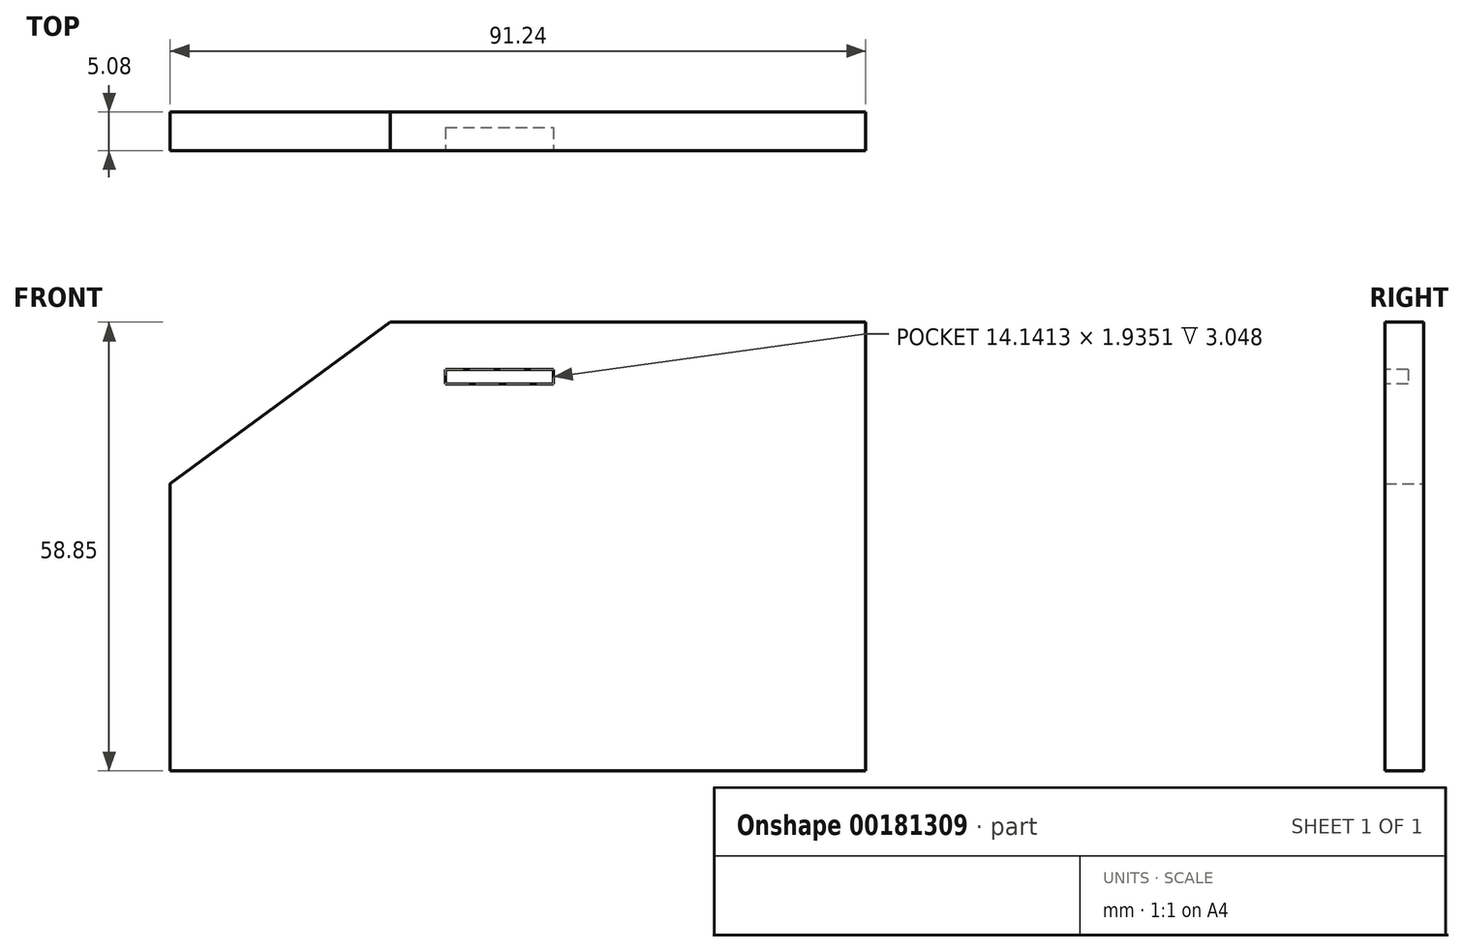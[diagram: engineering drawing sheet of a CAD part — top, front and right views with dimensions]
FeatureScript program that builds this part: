
annotation { "Feature Type Name" : "Feature", "Feature Type Description" : "" }
export const myFeature = defineFeature(function(context is Context, id is Id, definition is map)
    precondition{}
    {
        {
            var Q0;
            Q0=qCreatedBy(makeId("Front.planeOp"),FACE);
            var sketch = newSketch(context, id + "F0", { "sketchPlane" : qUnion([Q0])});
            skLineSegment(sketch, "E0", {"start": v(-53.99, 30.3) * mm, "end": v(-53.99, -7.33) * mm});
            skLineSegment(sketch, "E1", {"start": v(-53.99, 30.3) * mm, "end": v(4.93, 30.3) * mm});
            skLineSegment(sketch, "E2", {"start": v(4.93, 30.3) * mm, "end": v(4.93, -7.33) * mm});
            skLineSegment(sketch, "E3", {"start": v(-53.99, -7.33) * mm, "end": v(4.93, -7.33) * mm});
            skLineSegment(sketch, "E4", {"start": v(4.93, 30.3) * mm, "end": v(37.25, 30.3) * mm});
            skLineSegment(sketch, "E5", {"start": v(4.93, -7.33) * mm, "end": v(37.25, -7.33) * mm});
            skPoint(sketch, "E6.end.orphan", {"position": v(38.16, -7.33) * mm});
            skLineSegment(sketch, "E7", {"start": v(37.25, -7.33) * mm, "end": v(37.25, 30.3) * mm});
            skLineSegment(sketch, "E8", {"start": v(-53.99, 30.3) * mm, "end": v(-25.15, 51.52) * mm});
            skLineSegment(sketch, "E9", {"start": v(-25.15, 51.52) * mm, "end": v(4.93, 30.3) * mm});
            skLineSegment(sketch, "E10", {"start": v(37.25, 30.3) * mm, "end": v(37.25, 51.52) * mm});
            skPoint(sketch, "E11.end.orphan", {"position": v(32.6, 51.52) * mm});
            skLineSegment(sketch, "E12", {"start": v(37.25, 51.52) * mm, "end": v(-25.15, 51.52) * mm});
            skSolve(sketch);
        }
        {
            var Q0;
            Q0=makeQuery(id+"F0.imprint","IMPRINT",FACE,{"disambiguationData":[TD([[makeQuery(id+"F0.imprint","IMPRINT",EDGE,{"derivedFrom":sQuery(id+"F0.wireOp",EDGE,"E1")}),1.0]])]});
            var Q1;
            Q1=makeQuery(id+"F0.imprint","IMPRINT",FACE,{"disambiguationData":[TD([[makeQuery(id+"F0.imprint","IMPRINT",EDGE,{"derivedFrom":sQuery(id+"F0.wireOp",EDGE,"E4")}),1.0]])]});
            var Q2;
            Q2=makeQuery(id+"F0.imprint","IMPRINT",FACE,{"disambiguationData":[TD([[makeQuery(id+"F0.imprint","IMPRINT",EDGE,{"derivedFrom":sQuery(id+"F0.wireOp",EDGE,"E0")}),1.0]])]});
            var Q3;
            Q3=makeQuery(id+"F0.imprint","IMPRINT",FACE,{"disambiguationData":[TD([[makeQuery(id+"F0.imprint","IMPRINT",EDGE,{"derivedFrom":sQuery(id+"F0.wireOp",EDGE,"E2")}),1.0]])]});
            extrude(context, id + "F1", {"entities" : qUnion([Q0, Q1, Q2, Q3]), "depth" : 2.54 * mm, "hasSecondDirection" : true, "secondDirectionOppositeDirection" : true, "secondDirectionDepth" : 2.54 * mm});
        }
        {
            var Q0;
            Q0=makeQuery(id+"F1.opExtrude","SWEPT_FACE",FACE,{"disambiguationData":[OSD([sQuery(id+"F0.wireOp",EDGE,"E3"),sQuery(id+"F0.wireOp",EDGE,"E5")])]});
            var sketch = newSketch(context, id + "F2", { "sketchPlane" : qUnion([Q0])});
            skLineSegment(sketch, "E13.bottom", {"start": v(-49.45, 7.33) * mm, "end": v(-45.94, 7.33) * mm});
            skLineSegment(sketch, "E13.top", {"start": v(-49.45, 3.83) * mm, "end": v(-45.94, 3.83) * mm});
            skLineSegment(sketch, "E13.left", {"start": v(-49.45, 7.33) * mm, "end": v(-49.45, 3.83) * mm});
            skLineSegment(sketch, "E13.right", {"start": v(-45.94, 7.33) * mm, "end": v(-45.94, 3.83) * mm});
            skPoint(sketch, "E14.oppositeSnap0", {"position": v(-47.7, 3.83) * mm});
            skLineSegment(sketch, "E14.bottom", {"start": v(25.57, 7.33) * mm, "end": v(29.07, 7.33) * mm});
            skLineSegment(sketch, "E14.top", {"start": v(25.57, 3.83) * mm, "end": v(29.07, 3.83) * mm});
            skLineSegment(sketch, "E14.left", {"start": v(25.57, 7.33) * mm, "end": v(25.57, 3.83) * mm});
            skLineSegment(sketch, "E14.right", {"start": v(29.07, 7.33) * mm, "end": v(29.07, 3.83) * mm});
            skSolve(sketch);
        }
        {
            var Q0;
            Q0=makeQuery(id+"F2.imprint","IMPRINT",FACE,{"disambiguationData":[TD([[makeQuery(id+"F2.imprint","IMPRINT",EDGE,{"derivedFrom":sQuery(id+"F2.wireOp",EDGE,"E13.bottom")}),-1.0]])]});
            var Q1;
            Q1=makeQuery(id+"F2.imprint","IMPRINT",FACE,{"disambiguationData":[TD([[makeQuery(id+"F2.imprint","IMPRINT",EDGE,{"derivedFrom":sQuery(id+"F2.wireOp",EDGE,"E14.bottom")}),-1.0]])]});
            extrude(context, id + "F3", {"entities" : qUnion([Q0, Q1]), "operationType" : NewBodyOperationType.REMOVE, "oppositeDirection" : true, "depth" : 3.56 * mm});
        }
        {
            var Q0;
            Q0=makeQuery(id+"F1.opExtrude","CAP_FACE",FACE,{"disambiguationData":[OSD([sQuery(id+"F0.wireOp",EDGE,"E0"),sQuery(id+"F0.wireOp",EDGE,"E3"),sQuery(id+"F0.wireOp",EDGE,"E5"),sQuery(id+"F0.wireOp",EDGE,"E7"),sQuery(id+"F0.wireOp",EDGE,"E8"),sQuery(id+"F0.wireOp",EDGE,"E10"),sQuery(id+"F0.wireOp",EDGE,"E12")])],"isStart":false});
            var sketch = newSketch(context, id + "F4", { "sketchPlane" : qUnion([Q0])});
            skLineSegment(sketch, "E15.bottom", {"start": v(-9.68, 44.88) * mm, "end": v(0, 44.88) * mm});
            skLineSegment(sketch, "E15.top", {"start": v(-9.68, 45.92) * mm, "end": v(0, 45.92) * mm});
            skLineSegment(sketch, "E15.left", {"start": v(-9.68, 44.88) * mm, "end": v(-9.68, 45.92) * mm});
            skLineSegment(sketch, "E15.right", {"start": v(0, 44.88) * mm, "end": v(0, 45.92) * mm});
            skSolve(sketch);
        }
        {
            var Q0;
            Q0 = qSketchRegion(id + "F4", true);
            extrude(context, id + "F5", {"entities" : qUnion([Q0]), "operationType" : NewBodyOperationType.ADD, "oppositeDirection" : true, "depth" : 1.52 * mm});
        }
        {
            var Q0;
            Q0=makeQuery(id+"F1.opExtrude","CAP_FACE",FACE,{"disambiguationData":[OSD([sQuery(id+"F0.wireOp",EDGE,"E0"),sQuery(id+"F0.wireOp",EDGE,"E3"),sQuery(id+"F0.wireOp",EDGE,"E5"),sQuery(id+"F0.wireOp",EDGE,"E7"),sQuery(id+"F0.wireOp",EDGE,"E8"),sQuery(id+"F0.wireOp",EDGE,"E10"),sQuery(id+"F0.wireOp",EDGE,"E12")])],"isStart":false});
            var sketch = newSketch(context, id + "F6", { "sketchPlane" : qUnion([Q0])});
            skLineSegment(sketch, "E16.bottom", {"start": v(-17.86, 45.33) * mm, "end": v(-3.72, 45.33) * mm});
            skLineSegment(sketch, "E16.top", {"start": v(-17.86, 43.4) * mm, "end": v(-3.72, 43.4) * mm});
            skLineSegment(sketch, "E16.left", {"start": v(-17.86, 45.33) * mm, "end": v(-17.86, 43.4) * mm});
            skLineSegment(sketch, "E16.right", {"start": v(-3.72, 45.33) * mm, "end": v(-3.72, 43.4) * mm});
            skSolve(sketch);
        }
        {
            var Q0;
            Q0=makeQuery(id+"F6.imprint","IMPRINT",FACE,{"disambiguationData":[TD([[makeQuery(id+"F6.imprint","IMPRINT",EDGE,{"derivedFrom":sQuery(id+"F6.wireOp",EDGE,"E16.bottom")}),-1.0]])]});
            extrude(context, id + "F7", {"entities" : qUnion([Q0]), "operationType" : NewBodyOperationType.REMOVE, "oppositeDirection" : true, "depth" : 3.05 * mm});
        }
    });
